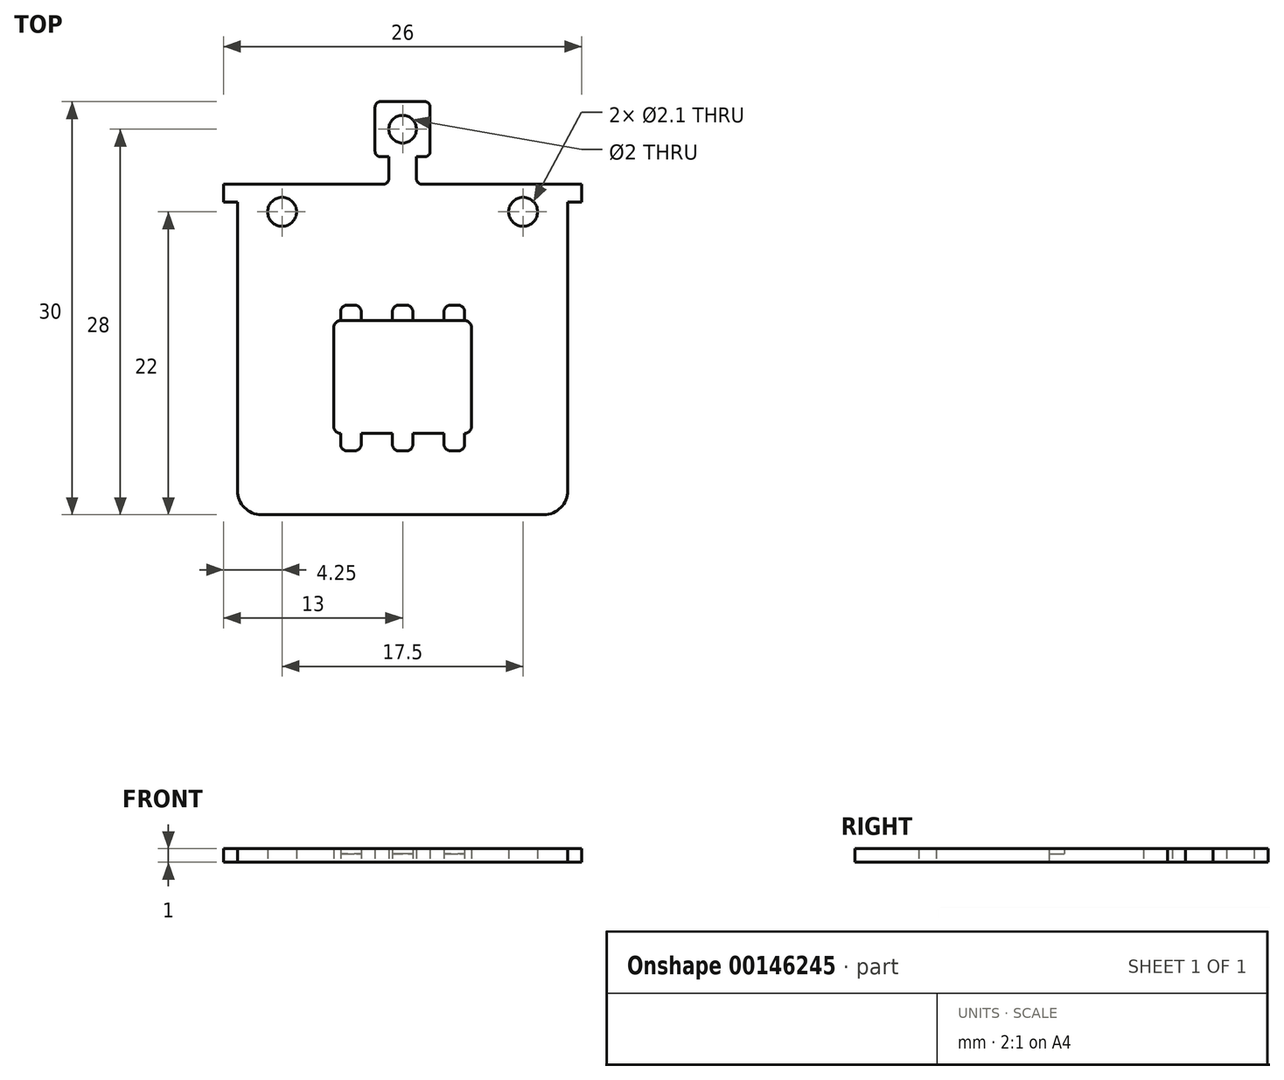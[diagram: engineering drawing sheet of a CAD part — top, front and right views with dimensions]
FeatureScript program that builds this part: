
annotation { "Feature Type Name" : "Feature", "Feature Type Description" : "" }
export const myFeature = defineFeature(function(context is Context, id is Id, definition is map)
    precondition{}
    {
        {
            var Q0;
            Q0=qCreatedBy(makeId("Top.planeOp"),FACE);
            var sketch = newSketch(context, id + "F0", { "sketchPlane" : qUnion([Q0])});
            skLineSegment(sketch, "E0.bottom", {"start": v(10.25, -11.35) * mm, "end": v(-10.25, -11.35) * mm});
            skLineSegment(sketch, "E0.left", {"start": v(12, -9.6) * mm, "end": v(12, 11.35) * mm});
            skLineSegment(sketch, "E0.right", {"start": v(-12, -9.6) * mm, "end": v(-12, 11.35) * mm});
            skPoint(sketch, "E0.middle", {"position": v(0, 0) * mm});
            skLineSegment(sketch, "E1", {"start": v(-12, 11.35) * mm, "end": v(-13, 11.35) * mm});
            skLineSegment(sketch, "E2", {"start": v(-13, 11.35) * mm, "end": v(-13, 12.65) * mm});
            skLineSegment(sketch, "E3", {"start": v(-13, 12.65) * mm, "end": v(-1.4, 12.65) * mm});
            skLineSegment(sketch, "E4", {"start": v(13, 12.65) * mm, "end": v(13, 11.35) * mm});
            skLineSegment(sketch, "E5", {"start": v(13, 11.35) * mm, "end": v(12, 11.35) * mm});
            skLineSegment(sketch, "E6", {"start": v(-1, 13.05) * mm, "end": v(-1, 14.65) * mm});
            skLineSegment(sketch, "E7", {"start": v(-1, 14.65) * mm, "end": v(-1.6, 14.65) * mm});
            skLineSegment(sketch, "E8", {"start": v(-2, 15.05) * mm, "end": v(-2, 18.25) * mm});
            skLineSegment(sketch, "E9", {"start": v(-1.6, 18.65) * mm, "end": v(1.6, 18.65) * mm});
            skLineSegment(sketch, "E10", {"start": v(2, 18.25) * mm, "end": v(2, 15.05) * mm});
            skLineSegment(sketch, "E11", {"start": v(1.6, 14.65) * mm, "end": v(1, 14.65) * mm});
            skLineSegment(sketch, "E12", {"start": v(1, 14.65) * mm, "end": v(1, 13.05) * mm});
            skPoint(sketch, "E13.visualSharp", {"position": v(-2, 18.65) * mm});
            skArc(sketch, "E13.filletArc", {"start": v(-1.6, 18.65) * mm, "mid": v(-1.88, 18.53) * mm, "end": v(-2, 18.25) * mm});
            skPoint(sketch, "E14.visualSharp", {"position": v(2, 18.65) * mm});
            skArc(sketch, "E14.filletArc", {"start": v(2, 18.25) * mm, "mid": v(1.88, 18.53) * mm, "end": v(1.6, 18.65) * mm});
            skPoint(sketch, "E15.visualSharp", {"position": v(2, 14.65) * mm});
            skArc(sketch, "E15.filletArc", {"start": v(1.6, 14.65) * mm, "mid": v(1.88, 14.77) * mm, "end": v(2, 15.05) * mm});
            skPoint(sketch, "E16.visualSharp", {"position": v(-2, 14.65) * mm});
            skArc(sketch, "E16.filletArc", {"start": v(-2, 15.05) * mm, "mid": v(-1.88, 14.77) * mm, "end": v(-1.6, 14.65) * mm});
            skLineSegment(sketch, "E17.trimOffspring", {"start": v(1.4, 12.65) * mm, "end": v(13, 12.65) * mm});
            skPoint(sketch, "E18.visualSharp", {"position": v(-1, 12.65) * mm});
            skArc(sketch, "E18.filletArc", {"start": v(-1.4, 12.65) * mm, "mid": v(-1.12, 12.77) * mm, "end": v(-1, 13.05) * mm});
            skPoint(sketch, "E19.visualSharp", {"position": v(1, 12.65) * mm});
            skArc(sketch, "E19.filletArc", {"start": v(1, 13.05) * mm, "mid": v(1.12, 12.77) * mm, "end": v(1.4, 12.65) * mm});
            skCircle(sketch, "E20", {"center": v(0, 16.65) * mm, "radius": 1 * mm});
            skPoint(sketch, "E21.visualSharp", {"position": v(-12, -11.35) * mm});
            skArc(sketch, "E21.filletArc", {"start": v(-12, -9.6) * mm, "mid": v(-11.49, -10.84) * mm, "end": v(-10.25, -11.35) * mm});
            skPoint(sketch, "E22.visualSharp", {"position": v(12, -11.35) * mm});
            skArc(sketch, "E22.filletArc", {"start": v(10.25, -11.35) * mm, "mid": v(11.49, -10.84) * mm, "end": v(12, -9.6) * mm});
            skLineSegment(sketch, "E23.bottom", {"start": v(-4.5, 2.75) * mm, "end": v(4.5, 2.75) * mm});
            skLineSegment(sketch, "E23.top", {"start": v(-4.5, -5.45) * mm, "end": v(4.5, -5.45) * mm});
            skLineSegment(sketch, "E23.left", {"start": v(-5, 2.25) * mm, "end": v(-5, -4.95) * mm});
            skLineSegment(sketch, "E23.right", {"start": v(5, 2.25) * mm, "end": v(5, -4.95) * mm});
            skPoint(sketch, "E23.middle", {"position": v(0, -1.35) * mm});
            skPoint(sketch, "E24.visualSharp", {"position": v(-5, 2.75) * mm});
            skArc(sketch, "E24.filletArc", {"start": v(-4.5, 2.75) * mm, "mid": v(-4.85, 2.6) * mm, "end": v(-5, 2.25) * mm});
            skPoint(sketch, "E25.visualSharp", {"position": v(5, 2.75) * mm});
            skArc(sketch, "E25.filletArc", {"start": v(5, 2.25) * mm, "mid": v(4.85, 2.6) * mm, "end": v(4.5, 2.75) * mm});
            skPoint(sketch, "E26.visualSharp", {"position": v(5, -5.45) * mm});
            skArc(sketch, "E26.filletArc", {"start": v(4.5, -5.45) * mm, "mid": v(4.85, -5.3) * mm, "end": v(5, -4.95) * mm});
            skPoint(sketch, "E27.visualSharp", {"position": v(-5, -5.45) * mm});
            skArc(sketch, "E27.filletArc", {"start": v(-5, -4.95) * mm, "mid": v(-4.85, -5.3) * mm, "end": v(-4.5, -5.45) * mm});
            skLineSegment(sketch, "E28.bottom", {"start": v(-0.25, 3.87) * mm, "end": v(0.25, 3.87) * mm});
            skLineSegment(sketch, "E28.top", {"start": v(-0.75, 2.75) * mm, "end": v(0.75, 2.75) * mm});
            skLineSegment(sketch, "E28.left", {"start": v(-0.75, 3.37) * mm, "end": v(-0.75, 2.75) * mm});
            skLineSegment(sketch, "E28.right", {"start": v(0.75, 3.37) * mm, "end": v(0.75, 2.75) * mm});
            skPoint(sketch, "E28.middle", {"position": v(0, 3.31) * mm});
            skLineSegment(sketch, "E29.bottom", {"start": v(-3.5, 3.87) * mm, "end": v(-4, 3.87) * mm});
            skLineSegment(sketch, "E29.top", {"start": v(-3, 2.75) * mm, "end": v(-4.5, 2.75) * mm});
            skLineSegment(sketch, "E29.left", {"start": v(-3, 3.37) * mm, "end": v(-3, 2.75) * mm});
            skLineSegment(sketch, "E29.right", {"start": v(-4.5, 3.37) * mm, "end": v(-4.5, 2.75) * mm});
            skPoint(sketch, "E29.middle", {"position": v(-3.75, 3.31) * mm});
            skLineSegment(sketch, "E30.bottom", {"start": v(4, 3.87) * mm, "end": v(3.5, 3.87) * mm});
            skLineSegment(sketch, "E30.top", {"start": v(4.5, 2.75) * mm, "end": v(3, 2.75) * mm});
            skLineSegment(sketch, "E30.left", {"start": v(4.5, 3.37) * mm, "end": v(4.5, 2.75) * mm});
            skLineSegment(sketch, "E30.right", {"start": v(3, 3.37) * mm, "end": v(3, 2.75) * mm});
            skPoint(sketch, "E30.middle", {"position": v(3.75, 3.31) * mm});
            skLineSegment(sketch, "E31.bottom", {"start": v(0.75, -5.45) * mm, "end": v(-0.75, -5.45) * mm});
            skLineSegment(sketch, "E31.top", {"start": v(0.25, -6.73) * mm, "end": v(-0.25, -6.73) * mm});
            skLineSegment(sketch, "E31.left", {"start": v(0.75, -5.45) * mm, "end": v(0.75, -6.23) * mm});
            skLineSegment(sketch, "E31.right", {"start": v(-0.75, -5.45) * mm, "end": v(-0.75, -6.23) * mm});
            skPoint(sketch, "E31.middle", {"position": v(0, -6.09) * mm});
            skLineSegment(sketch, "E32.bottom", {"start": v(4.5, -5.45) * mm, "end": v(3, -5.45) * mm});
            skLineSegment(sketch, "E32.top", {"start": v(4, -6.73) * mm, "end": v(3.5, -6.73) * mm});
            skLineSegment(sketch, "E32.left", {"start": v(4.5, -5.45) * mm, "end": v(4.5, -6.23) * mm});
            skLineSegment(sketch, "E32.right", {"start": v(3, -5.45) * mm, "end": v(3, -6.23) * mm});
            skPoint(sketch, "E32.middle", {"position": v(3.75, -6.09) * mm});
            skLineSegment(sketch, "E33.bottom", {"start": v(-4.5, -5.45) * mm, "end": v(-3, -5.45) * mm});
            skLineSegment(sketch, "E33.top", {"start": v(-4, -6.73) * mm, "end": v(-3.5, -6.73) * mm});
            skLineSegment(sketch, "E33.left", {"start": v(-4.5, -5.45) * mm, "end": v(-4.5, -6.23) * mm});
            skLineSegment(sketch, "E33.right", {"start": v(-3, -5.45) * mm, "end": v(-3, -6.23) * mm});
            skPoint(sketch, "E33.middle", {"position": v(-3.75, -6.09) * mm});
            skPoint(sketch, "E34.visualSharp", {"position": v(4.5, -6.73) * mm});
            skArc(sketch, "E34.filletArc", {"start": v(4, -6.73) * mm, "mid": v(4.35, -6.58) * mm, "end": v(4.5, -6.23) * mm});
            skPoint(sketch, "E35.visualSharp", {"position": v(3, -6.73) * mm});
            skArc(sketch, "E35.filletArc", {"start": v(3, -6.23) * mm, "mid": v(3.15, -6.58) * mm, "end": v(3.5, -6.73) * mm});
            skPoint(sketch, "E36.visualSharp", {"position": v(0.75, -6.73) * mm});
            skArc(sketch, "E36.filletArc", {"start": v(0.25, -6.73) * mm, "mid": v(0.6, -6.58) * mm, "end": v(0.75, -6.23) * mm});
            skPoint(sketch, "E37.visualSharp", {"position": v(-0.75, -6.73) * mm});
            skArc(sketch, "E37.filletArc", {"start": v(-0.75, -6.23) * mm, "mid": v(-0.6, -6.58) * mm, "end": v(-0.25, -6.73) * mm});
            skPoint(sketch, "E38.visualSharp", {"position": v(-3, -6.73) * mm});
            skArc(sketch, "E38.filletArc", {"start": v(-3.5, -6.73) * mm, "mid": v(-3.15, -6.58) * mm, "end": v(-3, -6.23) * mm});
            skPoint(sketch, "E39.visualSharp", {"position": v(-4.5, -6.73) * mm});
            skArc(sketch, "E39.filletArc", {"start": v(-4.5, -6.23) * mm, "mid": v(-4.35, -6.58) * mm, "end": v(-4, -6.73) * mm});
            skPoint(sketch, "E40.visualSharp", {"position": v(-4.5, 3.87) * mm});
            skArc(sketch, "E40.filletArc", {"start": v(-4, 3.87) * mm, "mid": v(-4.35, 3.73) * mm, "end": v(-4.5, 3.37) * mm});
            skPoint(sketch, "E41.visualSharp", {"position": v(-3, 3.87) * mm});
            skArc(sketch, "E41.filletArc", {"start": v(-3, 3.37) * mm, "mid": v(-3.15, 3.73) * mm, "end": v(-3.5, 3.87) * mm});
            skPoint(sketch, "E42.visualSharp", {"position": v(-0.75, 3.87) * mm});
            skArc(sketch, "E42.filletArc", {"start": v(-0.25, 3.87) * mm, "mid": v(-0.6, 3.73) * mm, "end": v(-0.75, 3.37) * mm});
            skPoint(sketch, "E43.visualSharp", {"position": v(0.75, 3.87) * mm});
            skArc(sketch, "E43.filletArc", {"start": v(0.75, 3.37) * mm, "mid": v(0.6, 3.73) * mm, "end": v(0.25, 3.87) * mm});
            skPoint(sketch, "E44.visualSharp", {"position": v(3, 3.87) * mm});
            skArc(sketch, "E44.filletArc", {"start": v(3.5, 3.87) * mm, "mid": v(3.15, 3.73) * mm, "end": v(3, 3.37) * mm});
            skPoint(sketch, "E45.visualSharp", {"position": v(4.5, 3.87) * mm});
            skArc(sketch, "E45.filletArc", {"start": v(4.5, 3.37) * mm, "mid": v(4.35, 3.73) * mm, "end": v(4, 3.87) * mm});
            skCircle(sketch, "E46", {"center": v(-8.75, 10.65) * mm, "radius": 1.05 * mm});
            skCircle(sketch, "E47", {"center": v(8.75, 10.65) * mm, "radius": 1.05 * mm});
            skSolve(sketch);
        }
        {
            var Q0;
            Q0=makeQuery(id+"F0.imprint","IMPRINT",FACE,{"disambiguationData":[TD([[makeQuery(id+"F0.imprint","IMPRINT",EDGE,{"derivedFrom":sQuery(id+"F0.wireOp",EDGE,"E0.bottom")}),-1.0]])]});
            var Q1;
            Q1=makeQuery(id+"F0.imprint","IMPRINT",FACE,{"disambiguationData":[TD([[makeQuery(id+"F0.imprint","IMPRINT",EDGE,{"derivedFrom":sQuery(id+"F0.wireOp",EDGE,"E29.bottom")}),1.0]])]});
            var Q2;
            Q2=makeQuery(id+"F0.imprint","IMPRINT",FACE,{"disambiguationData":[TD([[makeQuery(id+"F0.imprint","IMPRINT",EDGE,{"derivedFrom":sQuery(id+"F0.wireOp",EDGE,"E28.bottom")}),-1.0]])]});
            var Q3;
            Q3=makeQuery(id+"F0.imprint","IMPRINT",FACE,{"disambiguationData":[TD([[makeQuery(id+"F0.imprint","IMPRINT",EDGE,{"derivedFrom":sQuery(id+"F0.wireOp",EDGE,"E30.bottom")}),1.0]])]});
            var Q4;
            Q4=makeQuery(id+"F0.imprint","IMPRINT",FACE,{"disambiguationData":[TD([[makeQuery(id+"F0.imprint","IMPRINT",EDGE,{"derivedFrom":sQuery(id+"F0.wireOp",EDGE,"E32.bottom")}),1.0]])]});
            var Q5;
            Q5=makeQuery(id+"F0.imprint","IMPRINT",FACE,{"disambiguationData":[TD([[makeQuery(id+"F0.imprint","IMPRINT",EDGE,{"derivedFrom":sQuery(id+"F0.wireOp",EDGE,"E31.bottom")}),1.0]])]});
            var Q6;
            Q6=makeQuery(id+"F0.imprint","IMPRINT",FACE,{"disambiguationData":[TD([[makeQuery(id+"F0.imprint","IMPRINT",EDGE,{"derivedFrom":sQuery(id+"F0.wireOp",EDGE,"E33.bottom")}),-1.0]])]});
            extrude(context, id + "F1", {"entities" : qUnion([Q0, Q1, Q2, Q3, Q4, Q5, Q6]), "depth" : 0.6 * mm});
        }
        {
            var Q0;
            Q0 = qSketchRegion(id + "F0", true);
            extrude(context, id + "F2", {"entities" : qUnion([Q0]), "operationType" : NewBodyOperationType.ADD, "depth" : 1 * mm});
        }
    });
